# Revit family: QF_ELECTROLUXPROFESSIONAL_341002_D01H4
name_source: partatom
category: Attrezzature speciali
revit_build: Autodesk Revit 2018 (Build: 20181011_1500(x64)
units: mm (PartAtom-declared; Revit-internal decimal feet)

## family parameters
Basato su piano di lavoro = No
Condiviso = No
Punto di calcolo locali = No
Quota connettore circolare = Usa diametro
Sempre verticale = Sì
Taglio con vuoti quando caricato = No
Tipo di parte = Normale

## types (2) — shared parameters
Accessory = Sì
Compressed Air Pressure = 0.0 Pa
Compressed Air Size = 0 mm
Compressed Air Volume = 0.0 L/s
Condensate Return Size = 0 mm
Depth Actual = 620 mm  [stored 2.03412 ft]
Gas Input Pressure = 0
Gas Size = 0 mm
Height Actual = 260 mm  [stored 0.853018 ft]
Hot Water Size = 0 mm
Length Actual = 1420 mm
Refrigerant Compressor Remote = Sì
Steam Supply Maximum Pressure = 0.0 Pa
Steam Supply Minimum Pressure = 0.0 Pa
Steam Supply Size = 0 mm
zero-valued in all types: Gas KW, Refrigeration Liquid Line Size, Refrigeration Suction Line Size, Steam Consumption per Hour

## per-type parameters (varying)
| type | Cold Water Size | Cycle | Descrizione | Direct Waste Size | HP | Item Number | Modello | Phase | Produttore | URL | URL Manufacturer | Volts | Watts | Weight |
| 341002.rfa | 0 mm | 0 Hz |  | 0 mm |  |  |  | 0 |  |  |  | 0 V | 0 W | 0.00 kg |
| Standard | 13 mm | 50 Hz | DROP-IN BAIN-MARIE, WATER, SINGLE WELL, 4GN | 25 mm | 4 HP | 341002 | D01H4 | 1 | Electrolux Professional | https://www.electroluxprofessional.com | https://www.electroluxprofessional.com | 220 V | 3020 W | 34.60 kg |

note: source unit labels omitted for Gas Input Pressure — the stored unit's dimension contradicts the parameter name (converter mislabeling)

note: [stored X ft] marks values corroborated as IEEE doubles in the binary element streams (Revit-internal decimal feet)

## geometry (parser evidence)
native form markers: Sweep x7
no freeform markers — native parametric forms only
